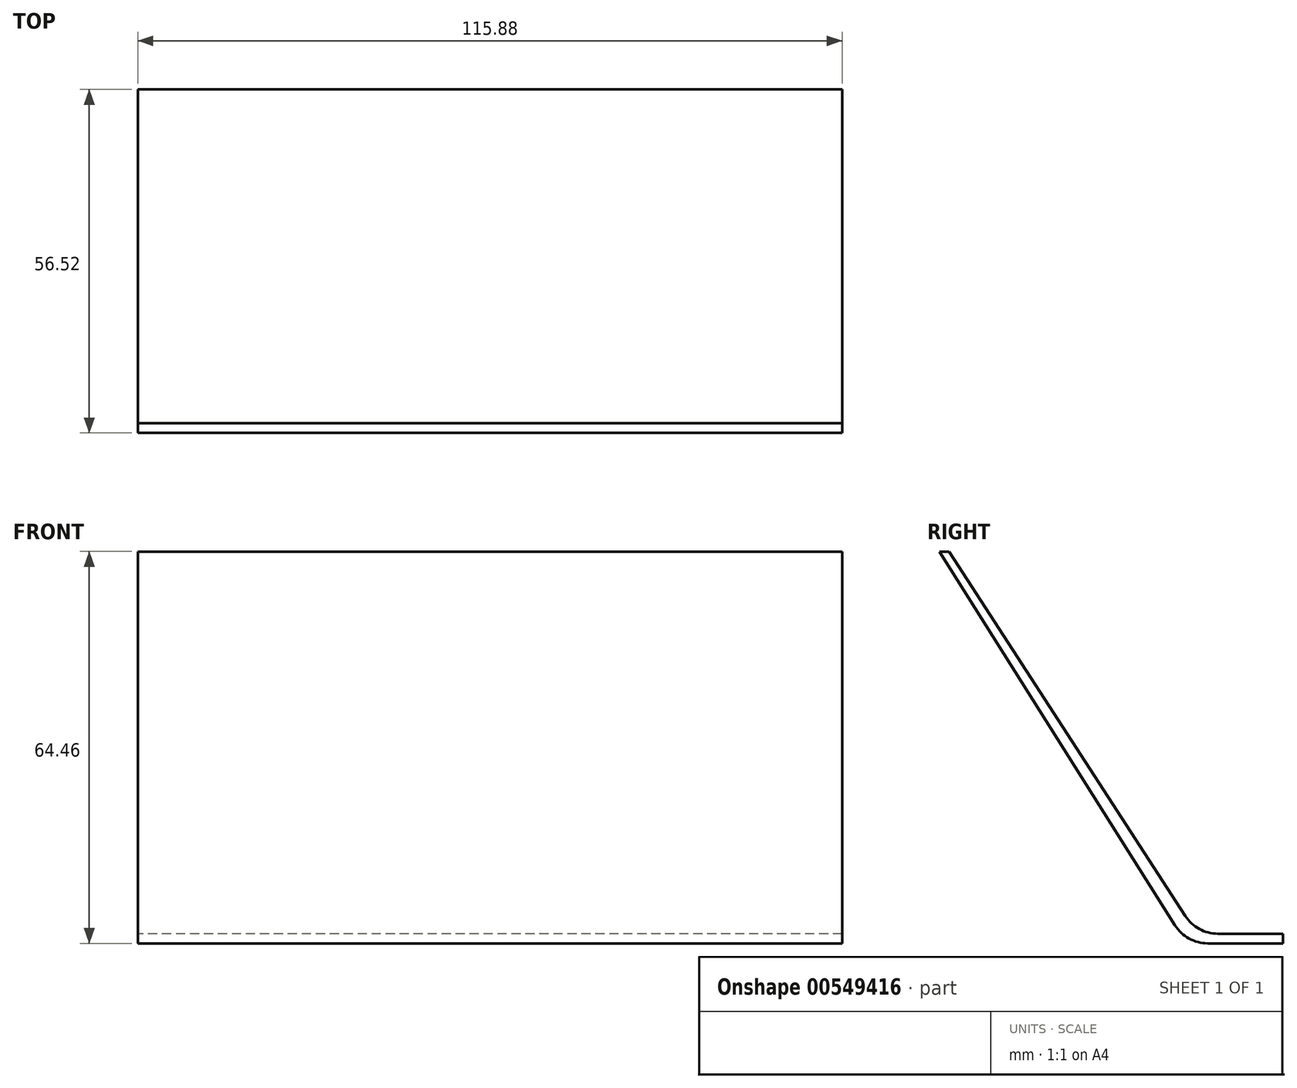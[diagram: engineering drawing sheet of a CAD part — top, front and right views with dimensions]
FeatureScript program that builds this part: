
annotation { "Feature Type Name" : "Feature", "Feature Type Description" : "" }
export const myFeature = defineFeature(function(context is Context, id is Id, definition is map)
    precondition{}
    {
        {
            var Q0;
            Q0=qCreatedBy(makeId("Right.planeOp"),FACE);
            var sketch = newSketch(context, id + "F0", { "sketchPlane" : qUnion([Q0])});
            skLineSegment(sketch, "E0", {"start": v(15.88, 0) * mm, "end": v(3.5, 0) * mm});
            skLineSegment(sketch, "E1", {"start": v(-1.87, 2.96) * mm, "end": v(-40.64, 64.46) * mm});
            skPoint(sketch, "E2.visualSharp", {"position": v(0, 0) * mm});
            skArc(sketch, "E2.filletArc", {"start": v(-1.87, 2.96) * mm, "mid": v(0.44, 0.79) * mm, "end": v(3.5, 0) * mm});
            skLineSegment(sketch, "E3", {"start": v(15.88, 0) * mm, "end": v(15.88, 1.59) * mm});
            skLineSegment(sketch, "E4", {"start": v(-40.64, 64.46) * mm, "end": v(-39.05, 64.46) * mm});
            skPoint(sketch, "E5.visualSharp", {"position": v(3.5, 2.96) * mm});
            skLineSegment(sketch, "E6", {"start": v(15.88, 1.59) * mm, "end": v(5.16, 1.59) * mm});
            skLineSegment(sketch, "E7", {"start": v(-0.16, 4.48) * mm, "end": v(-39.05, 64.46) * mm});
            skPoint(sketch, "E8.visualSharp", {"position": v(1.71, 1.59) * mm});
            skArc(sketch, "E8.filletArc", {"start": v(-0.16, 4.48) * mm, "mid": v(2.13, 2.36) * mm, "end": v(5.16, 1.59) * mm});
            skSolve(sketch);
        }
        {
            var Q0;
            Q0=makeQuery(id+"F0.imprint","IMPRINT",FACE,{"disambiguationData":[TD([[makeQuery(id+"F0.imprint","IMPRINT",EDGE,{"derivedFrom":sQuery(id+"F0.wireOp",EDGE,"E0")}),-1.0]])]});
            extrude(context, id + "F1", {"entities" : qUnion([Q0]), "endBound" : BoundingType.SYMMETRIC, "depth" : 115.89 * mm, "offsetDistance" : 25.4 * mm});
        }
    });
